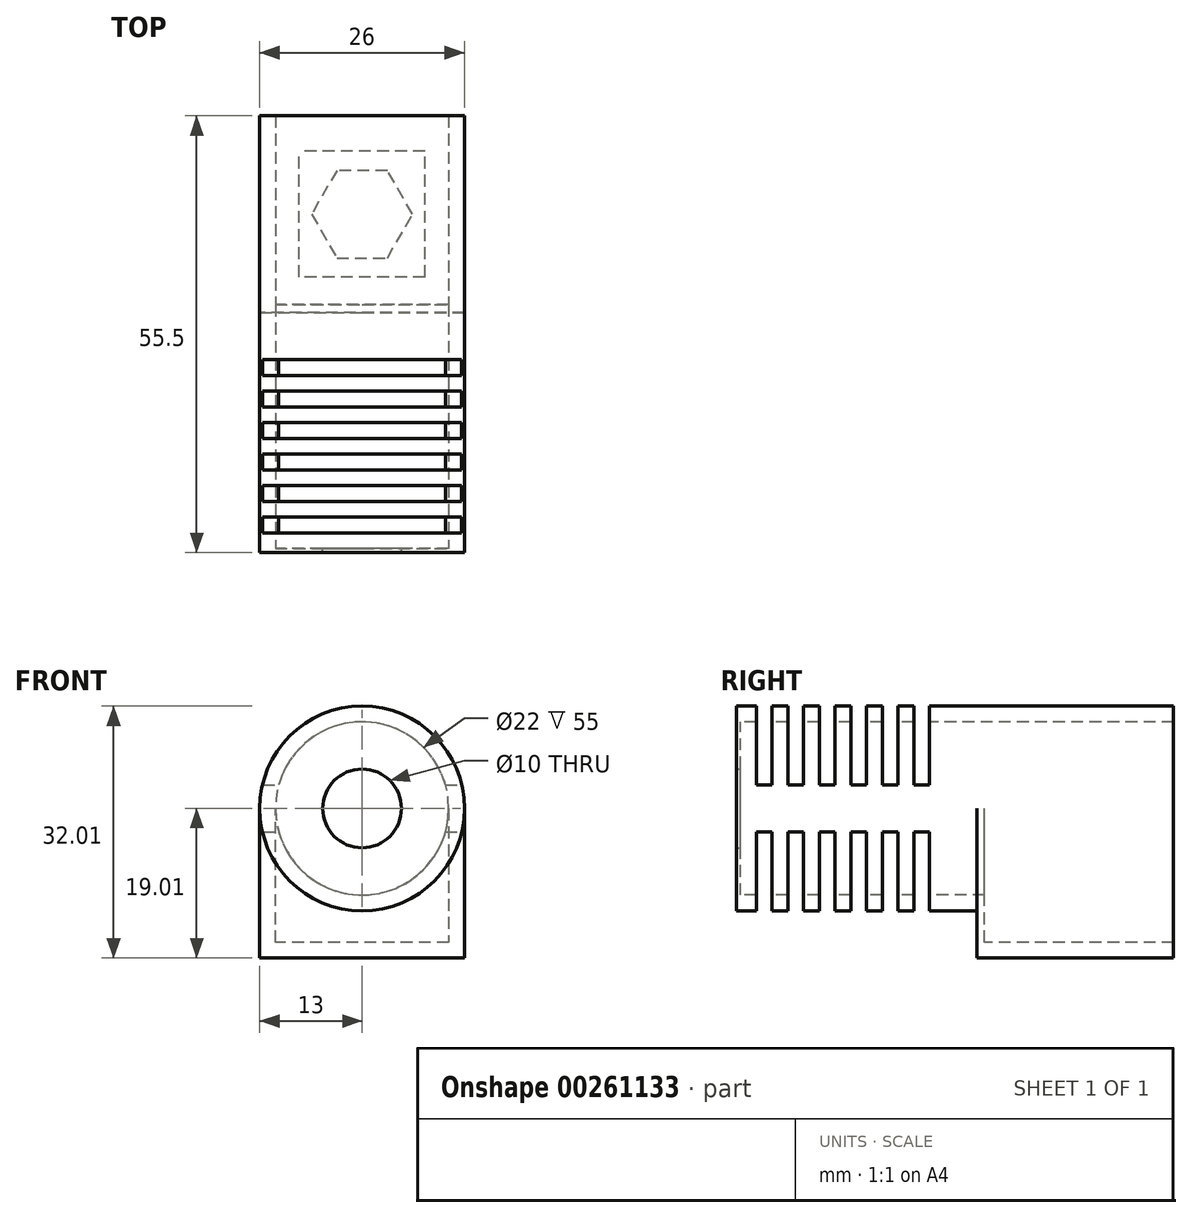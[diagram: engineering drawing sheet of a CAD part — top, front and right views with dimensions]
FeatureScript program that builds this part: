
annotation { "Feature Type Name" : "Feature", "Feature Type Description" : "" }
export const myFeature = defineFeature(function(context is Context, id is Id, definition is map)
    precondition{}
    {
        {
            var Q0;
            Q0=qCreatedBy(makeId("Front.planeOp"),FACE);
            var sketch = newSketch(context, id + "F0", { "sketchPlane" : qUnion([Q0])});
            skCircle(sketch, "E0", {"center": v(0, 0) * mm, "radius": 13 * mm});
            skCircle(sketch, "E1", {"center": v(0, 0) * mm, "radius": 11 * mm});
            skSolve(sketch);
        }
        {
            var Q0;
            Q0=qSketchRegion(id+"F0",true);
            extrude(context, id + "F1", {"entities" : qUnion([Q0]), "oppositeDirection" : true, "depth" : 30 * mm});
        }
        {
            var Q0;
            Q0=qCreatedBy(makeId("Front.planeOp"),FACE);
            var sketch = newSketch(context, id + "F2", { "sketchPlane" : qUnion([Q0])});
            skCircle(sketch, "E2", {"center": v(0, 0) * mm, "radius": 13 * mm});
            skCircle(sketch, "E3", {"center": v(0, 0) * mm, "radius": 5 * mm});
            skSolve(sketch);
        }
        {
            var Q0;
            Q0=qSketchRegion(id+"F2",true);
            extrude(context, id + "F3", {"entities" : qUnion([Q0]), "operationType" : NewBodyOperationType.ADD, "depth" : 0.5 * mm});
        }
        {
            var Q0;
            Q0=qCreatedBy(makeId("Top.planeOp"),FACE);
            cPlane(context, id + "F4", {"entities" : qUnion([Q0]), "cplaneType" : CPlaneType.OFFSET, "offset" : 13 * mm, "width" : 150 * mm, "height" : 150 * mm});
        }
        {
            var Q0;
            Q0=qCreatedBy(id+"F4.planeOp",FACE);
            var sketch = newSketch(context, id + "F5", { "sketchPlane" : qUnion([Q0])});
            skLineSegment(sketch, "E4", {"start": v(-13, 0) * mm, "end": v(13, 0) * mm});
            skLineSegment(sketch, "E5", {"start": v(-13, 2) * mm, "end": v(-13, 4) * mm});
            skLineSegment(sketch, "E6", {"start": v(-13, 26) * mm, "end": v(13, 26) * mm});
            skLineSegment(sketch, "E7", {"start": v(13, 24) * mm, "end": v(13, 22) * mm});
            skLineSegment(sketch, "E8.0.1.0", {"start": v(-13, 2) * mm, "end": v(13, 2) * mm});
            skLineSegment(sketch, "E8.0.2.0", {"start": v(-13, 4) * mm, "end": v(13, 4) * mm});
            skLineSegment(sketch, "E8.0.3.0", {"start": v(-13, 6) * mm, "end": v(13, 6) * mm});
            skLineSegment(sketch, "E8.0.4.0", {"start": v(-13, 8) * mm, "end": v(13, 8) * mm});
            skLineSegment(sketch, "E8.0.5.0", {"start": v(-13, 10) * mm, "end": v(13, 10) * mm});
            skLineSegment(sketch, "E8.0.6.0", {"start": v(-13, 12) * mm, "end": v(13, 12) * mm});
            skLineSegment(sketch, "E8.0.7.0", {"start": v(-13, 14) * mm, "end": v(13, 14) * mm});
            skLineSegment(sketch, "E8.0.8.0", {"start": v(-13, 16) * mm, "end": v(13, 16) * mm});
            skLineSegment(sketch, "E8.0.9.0", {"start": v(-13, 18) * mm, "end": v(13, 18) * mm});
            skLineSegment(sketch, "E8.0.10.0", {"start": v(-13, 20) * mm, "end": v(13, 20) * mm});
            skLineSegment(sketch, "E8.0.11.0", {"start": v(-13, 22) * mm, "end": v(13, 22) * mm});
            skLineSegment(sketch, "E8.0.12.0", {"start": v(-13, 24) * mm, "end": v(13, 24) * mm});
            skLineSegment(sketch, "E9.trimOffspring", {"start": v(-13, 22) * mm, "end": v(-13, 24) * mm});
            skLineSegment(sketch, "E10.trimOffspring", {"start": v(13, 20) * mm, "end": v(13, 18) * mm});
            skLineSegment(sketch, "E11.trimOffspring", {"start": v(-13, 18) * mm, "end": v(-13, 20) * mm});
            skLineSegment(sketch, "E12.trimOffspring", {"start": v(13, 16) * mm, "end": v(13, 14) * mm});
            skLineSegment(sketch, "E13.trimOffspring", {"start": v(-13, 14) * mm, "end": v(-13, 16) * mm});
            skLineSegment(sketch, "E14.trimOffspring", {"start": v(13, 12) * mm, "end": v(13, 10) * mm});
            skLineSegment(sketch, "E15.trimOffspring", {"start": v(-13, 10) * mm, "end": v(-13, 12) * mm});
            skLineSegment(sketch, "E16.trimOffspring", {"start": v(13, 8) * mm, "end": v(13, 6) * mm});
            skLineSegment(sketch, "E17.trimOffspring", {"start": v(-13, 6) * mm, "end": v(-13, 8) * mm});
            skLineSegment(sketch, "E18.trimOffspring", {"start": v(13, 4) * mm, "end": v(13, 2) * mm});
            skLineSegment(sketch, "E19", {"start": v(0, -4) * mm, "end": v(0, -5) * mm});
            skSolve(sketch);
        }
        {
            var Q0;
            Q0=qSketchRegion(id+"F5",true);
            extrude(context, id + "F6", {"entities" : qUnion([Q0]), "operationType" : NewBodyOperationType.REMOVE, "oppositeDirection" : true, "depth" : 10 * mm});
        }
        {
            var Q0;
            Q0=qCreatedBy(makeId("Top.planeOp"),FACE);
            cPlane(context, id + "F7", {"entities" : qUnion([Q0]), "cplaneType" : CPlaneType.OFFSET, "offset" : 13 * mm, "oppositeDirection" : true, "width" : 150 * mm, "height" : 150 * mm});
        }
        {
            var Q0;
            Q0=qCreatedBy(id+"F7.planeOp",FACE);
            var sketch = newSketch(context, id + "F8", { "sketchPlane" : qUnion([Q0])});
            skLineSegment(sketch, "E20", {"start": v(13, 2) * mm, "end": v(13, 4) * mm});
            skLineSegment(sketch, "E21", {"start": v(-13, 2) * mm, "end": v(-13, 4) * mm});
            skLineSegment(sketch, "E22.0.1.0", {"start": v(-13, 2) * mm, "end": v(13, 2) * mm});
            skLineSegment(sketch, "E22.0.2.0", {"start": v(-13, 4) * mm, "end": v(13, 4) * mm});
            skLineSegment(sketch, "E22.0.3.0", {"start": v(-13, 6) * mm, "end": v(13, 6) * mm});
            skLineSegment(sketch, "E22.0.4.0", {"start": v(-13, 8) * mm, "end": v(13, 8) * mm});
            skLineSegment(sketch, "E22.0.5.0", {"start": v(-13, 10) * mm, "end": v(13, 10) * mm});
            skLineSegment(sketch, "E22.0.6.0", {"start": v(-13, 12) * mm, "end": v(13, 12) * mm});
            skLineSegment(sketch, "E22.0.7.0", {"start": v(-13, 14) * mm, "end": v(13, 14) * mm});
            skLineSegment(sketch, "E22.0.8.0", {"start": v(-13, 16) * mm, "end": v(13, 16) * mm});
            skLineSegment(sketch, "E22.0.9.0", {"start": v(-13, 18) * mm, "end": v(13, 18) * mm});
            skLineSegment(sketch, "E22.0.10.0", {"start": v(-13, 20) * mm, "end": v(13, 20) * mm});
            skLineSegment(sketch, "E22.0.11.0", {"start": v(-13, 22) * mm, "end": v(13, 22) * mm});
            skLineSegment(sketch, "E22.0.12.0", {"start": v(-13, 24) * mm, "end": v(13, 24) * mm});
            skLineSegment(sketch, "E23.trimOffspring", {"start": v(-13, 6) * mm, "end": v(-13, 8) * mm});
            skLineSegment(sketch, "E24.trimOffspring", {"start": v(13, 6) * mm, "end": v(13, 8) * mm});
            skLineSegment(sketch, "E25.trimOffspring", {"start": v(-13, 4) * mm, "end": v(-13, 2) * mm});
            skLineSegment(sketch, "E26.trimOffspring", {"start": v(-13, 8) * mm, "end": v(-13, 6) * mm});
            skLineSegment(sketch, "E27.trimOffspring", {"start": v(-13, 10) * mm, "end": v(-13, 12) * mm});
            skLineSegment(sketch, "E28.trimOffspring", {"start": v(13, 10) * mm, "end": v(13, 12) * mm});
            skLineSegment(sketch, "E29.trimOffspring", {"start": v(-13, 12) * mm, "end": v(-13, 10) * mm});
            skLineSegment(sketch, "E30.trimOffspring", {"start": v(-13, 14) * mm, "end": v(-13, 16) * mm});
            skLineSegment(sketch, "E31.trimOffspring", {"start": v(13, 14) * mm, "end": v(13, 16) * mm});
            skLineSegment(sketch, "E32.trimOffspring", {"start": v(-13, 16) * mm, "end": v(-13, 14) * mm});
            skLineSegment(sketch, "E33.trimOffspring", {"start": v(13, 18) * mm, "end": v(13, 20) * mm});
            skLineSegment(sketch, "E34.trimOffspring", {"start": v(-13, 20) * mm, "end": v(-13, 18) * mm});
            skLineSegment(sketch, "E35.trimOffspring", {"start": v(-13, 22) * mm, "end": v(-13, 24) * mm});
            skLineSegment(sketch, "E36.trimOffspring", {"start": v(13, 22) * mm, "end": v(13, 24) * mm});
            skLineSegment(sketch, "E37.trimOffspring", {"start": v(-13, 24) * mm, "end": v(-13, 22) * mm});
            skSolve(sketch);
        }
        {
            var Q0;
            Q0=qSketchRegion(id+"F8",true);
            extrude(context, id + "F9", {"entities" : qUnion([Q0]), "operationType" : NewBodyOperationType.REMOVE, "depth" : 10 * mm});
        }
        {
            var Q0;
            Q0=makeQuery(id+"F1.opExtrude","CAP_FACE",FACE,{"disambiguationData":[OSD([sQuery(id+"F0.wireOp",EDGE,"E0"),sQuery(id+"F0.wireOp",EDGE,"E1")])],"isStart":false});
            var sketch = newSketch(context, id + "F10", { "sketchPlane" : qUnion([Q0])});
            skArc(sketch, "E38", {"start": v(11, -6.93) * mm, "mid": v(0, 13) * mm, "end": v(-11, -6.93) * mm});
            skLineSegment(sketch, "E39", {"start": v(-13, 0) * mm, "end": v(-13, -19) * mm});
            skLineSegment(sketch, "E40", {"start": v(-13, -19) * mm, "end": v(13, -19) * mm});
            skLineSegment(sketch, "E41", {"start": v(13, -19) * mm, "end": v(13, 0) * mm});
            skLineSegment(sketch, "E42", {"start": v(-11, 0) * mm, "end": v(-11, -17) * mm});
            skLineSegment(sketch, "E43", {"start": v(-11, -17) * mm, "end": v(11, -17) * mm});
            skLineSegment(sketch, "E44", {"start": v(11, -17) * mm, "end": v(11, 0) * mm});
            skSolve(sketch);
        }
        {
            var Q0;
            {var subQ0=sQuery(id+"F10.wireOp",EDGE,"E38");var subQ1=makeQuery(id+"F10.imprint","INTERSECT",VERTEX,{"derivedFrom":[subQ0,sQuery(id+"F10.wireOp",EDGE,"E39")]});Q0=makeQuery(id+"F10.imprint","IMPRINT",FACE,{"disambiguationData":[TD([[makeQuery(id+"F10.imprint","IMPRINT",EDGE,{"disambiguationData":[TD([[subQ1,-1.0]])],"derivedFrom":subQ0}),-1.0]])]});}
            var Q1;
            {var subQ0=sQuery(id+"F10.wireOp",EDGE,"E39");Q1=makeQuery(id+"F10.imprint","IMPRINT",FACE,{"disambiguationData":[TD([[makeQuery(id+"F10.imprint","IMPRINT",EDGE,{"derivedFrom":subQ0}),1.0]])]});}
            extrude(context, id + "F11", {"entities" : qUnion([Q0, Q1]), "operationType" : NewBodyOperationType.ADD, "depth" : 25 * mm});
        }
        {
            var Q0;
            Q0=makeQuery(id+"F1.opExtrude","CAP_FACE",FACE,{"disambiguationData":[OSD([sQuery(id+"F0.wireOp",EDGE,"E0"),sQuery(id+"F0.wireOp",EDGE,"E1")])],"isStart":false});
            var sketch = newSketch(context, id + "F12", { "sketchPlane" : qUnion([Q0])});
            skCircle(sketch, "E45", {"center": v(0, 0) * mm, "radius": 13 * mm});
            skLineSegment(sketch, "E46", {"start": v(-13, 0) * mm, "end": v(-13, -19) * mm});
            skLineSegment(sketch, "E47", {"start": v(-13, -19) * mm, "end": v(13, -19) * mm});
            skLineSegment(sketch, "E48", {"start": v(13, -19) * mm, "end": v(13, 0) * mm});
            skSolve(sketch);
        }
        {
            var Q0;
            {var subQ0=sQuery(id+"F12.wireOp",EDGE,"E46");Q0=makeQuery(id+"F12.imprint","IMPRINT",FACE,{"disambiguationData":[TD([[makeQuery(id+"F12.imprint","IMPRINT",EDGE,{"derivedFrom":subQ0}),1.0]])]});}
            var Q1;
            {var subQ1=sQuery(id+"F0.wireOp",EDGE,"E1");Q1=makeQuery(id+"F12.imprint","IMPRINT",FACE,{"disambiguationData":[TD([[makeQuery(id+"F12.imprint","IMPRINT",EDGE,{"derivedFrom":makeQuery(id+"F1.opExtrude","CAP_EDGE",EDGE,{"disambiguationData":[OSD([subQ1])],"isStart":false})}),1.0]])]});}
            extrude(context, id + "F13", {"entities" : qUnion([Q0, Q1]), "operationType" : NewBodyOperationType.ADD, "depth" : 1 * mm});
        }
        {
            var Q0;
            Q0=makeQuery(id+"F11.opExtrude","SWEPT_FACE",FACE,{"disambiguationData":[OSD([sQuery(id+"F10.wireOp",EDGE,"E40")])]});
            var sketch = newSketch(context, id + "F14", { "sketchPlane" : qUnion([Q0])});
            skCircle(sketch, "E49.cCircle", {"center": v(0, -42.5) * mm, "radius": 5.56 * mm, "construction": true});
            skLineSegment(sketch, "E49.0", {"start": v(3.2, -36.94) * mm, "end": v(6.42, -42.5) * mm});
            skLineSegment(sketch, "E49.1", {"start": v(6.42, -42.5) * mm, "end": v(3.2, -48.06) * mm});
            skLineSegment(sketch, "E49.2", {"start": v(3.2, -48.06) * mm, "end": v(-3.2, -48.06) * mm});
            skLineSegment(sketch, "E49.3", {"start": v(-3.2, -48.06) * mm, "end": v(-6.42, -42.5) * mm});
            skLineSegment(sketch, "E49.4", {"start": v(-6.42, -42.5) * mm, "end": v(-3.2, -36.94) * mm});
            skLineSegment(sketch, "E49.5", {"start": v(-3.2, -36.94) * mm, "end": v(3.2, -36.94) * mm});
            skPoint(sketch, "E49.0.midPoint", {"position": v(4.81, -39.72) * mm});
            skPoint(sketch, "E50", {"position": v(-13, -30) * mm});
            skPoint(sketch, "E51", {"position": v(-13, -55) * mm});
            skLineSegment(sketch, "E52.bottom", {"start": v(8, -34.5) * mm, "end": v(-8, -34.5) * mm});
            skLineSegment(sketch, "E52.top", {"start": v(8, -50.5) * mm, "end": v(-8, -50.5) * mm});
            skLineSegment(sketch, "E52.left", {"start": v(8, -34.5) * mm, "end": v(8, -50.5) * mm});
            skLineSegment(sketch, "E52.right", {"start": v(-8, -34.5) * mm, "end": v(-8, -50.5) * mm});
            skSolve(sketch);
        }
        {
            var Q0;
            Q0 = qSketchRegion(id + "F14", true);
            extrude(context, id + "F15", {"entities" : qUnion([Q0]), "operationType" : NewBodyOperationType.ADD, "depth" : 7 / 812.8 * mm});
        }
    });
